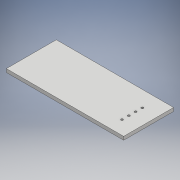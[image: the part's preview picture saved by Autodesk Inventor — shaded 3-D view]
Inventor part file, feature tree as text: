
AUTODESK INVENTOR PART (.ipt)
format: ipt  version: 2018.3 (Build 223284000, 284)  size: 98,816 bytes
history: native  units: mm
features: sketch x2, extrude x1, hole x1
ambient origin geometry x8: Origin, YZ Plane, XZ Plane, XY Plane, X Axis, Y Axis, Z Axis, Center Point
bodies: Solid1 (feature_tree)
feature tree (4):
  extrude  "Extrusion1"  Depth=34.5mm
  hole  "Hole1"  [1 undecoded]
  sketch  "Sketch1"  dims[d0=14.7mm d1=34.5mm]
  sketch  "Sketch3"  dims[d2=1.0mm d3=0.0mm d9=0.65mm d10=6.0mm d11=4.0mm d12=2.0mm d13=90.0deg d14=8.0mm d15=20.594885mm]
note: 1 required parameter value undecoded (feature->parameter linkage not recoverable at this tier; creation-order binding heuristic only, values carry confidence <= 0.55)
